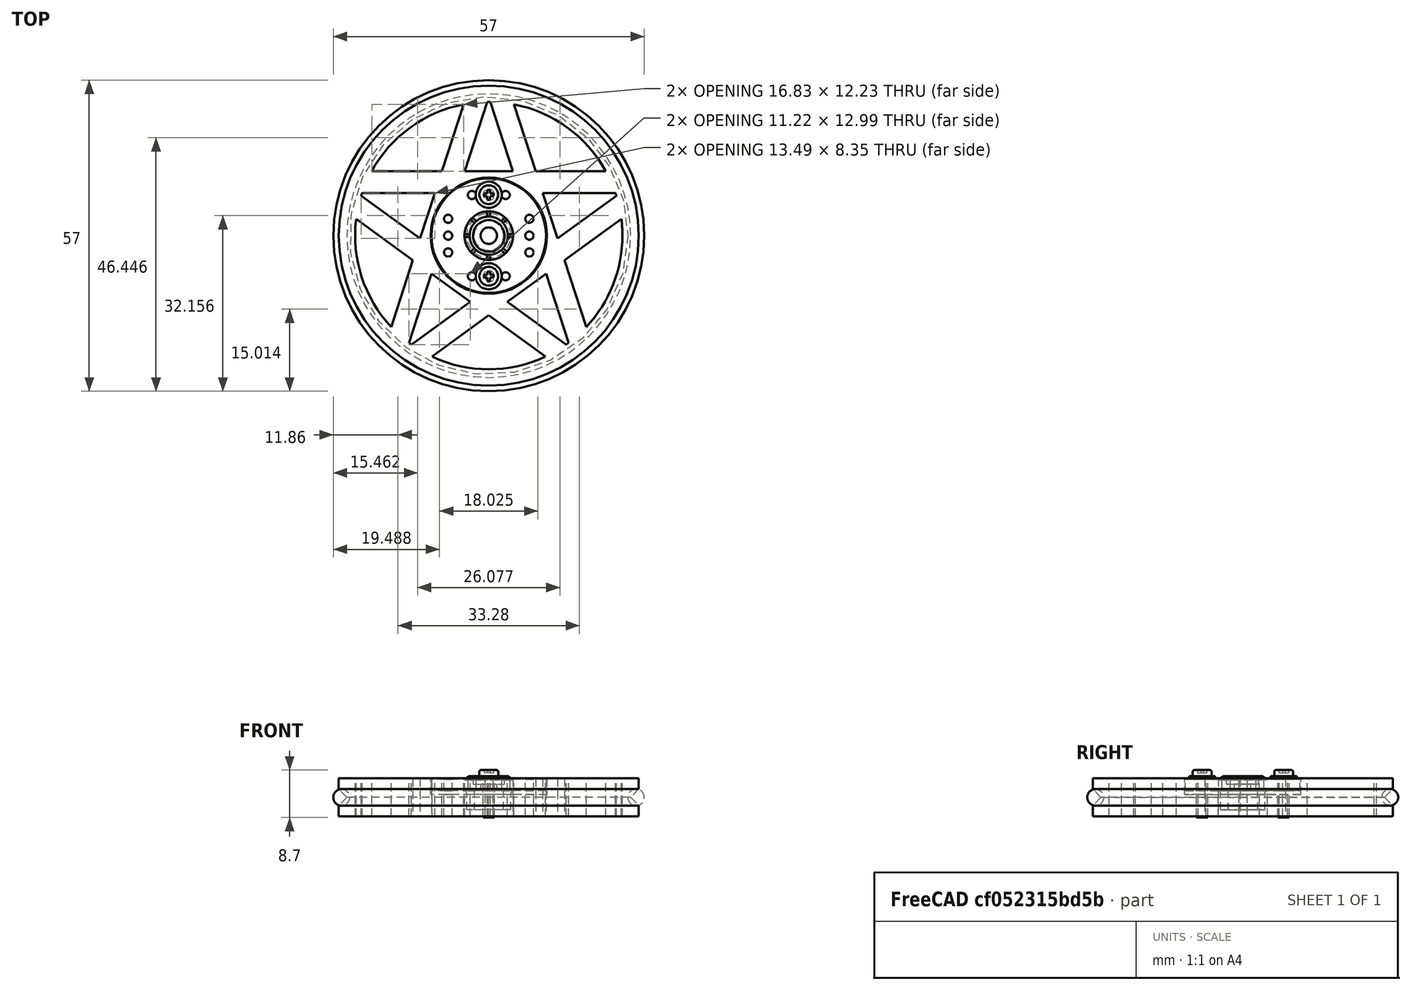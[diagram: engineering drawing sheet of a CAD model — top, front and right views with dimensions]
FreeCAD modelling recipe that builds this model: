
FCSTD DOCUMENT  (FreeCAD 0.14R3702 (Git))
Label: Miniskybot-wheel-pentacle-futaba3003-assembly
License: CC-BY 3.0
LicenseURL: http://creativecommons.org/licenses/by/3.0/
objects: Part::Feature×4, Part::Torus×1, Part::Compound×1
note: 6 computed .brp shape members not serialized (recipe doc carries the construction recipe); baked Part::Feature solids carry a one-line shape summary decoded from their .brp

FEATURE [Part::Feature] PolarPattern  label="Wheel-pentacle"
  shape: bbox 55 x 55 x 7 mm, 49 faces (baked)
FEATURE [Part::Torus] Torus  label="o-ring"
  Angle1 = -180
  Angle2 = 180
  Angle3 = 360
  Radius1 = 27
  Radius2 = 1.5
FEATURE [Part::Feature] Fillet  label="bolt-1"
  Placement = pos=(0,7.5,3.3) rot=(0,0,1;0rad)
  shape: bbox 4.8 x 4.8 x 8.7 mm, 21 faces (baked)
FEATURE [Part::Feature] Fillet001  label="servo-rounded-horn"
  Placement = pos=(0,0,-2.3) rot=(1,0,0;1.5708rad)
  shape: bbox 21 x 21 x 6.2 mm, 65 faces (baked)
FEATURE [Part::Feature] Fillet002  label="bolt-002"
  Placement = pos=(0,-7.45,3.3) rot=(0,0,1;0rad)
  shape: bbox 4.8 x 4.8 x 8.7 mm, 21 faces (baked)
FEATURE [Part::Compound] Compound  label="Miniskybot-wheel-pentacle-futaba3003-assembly-final"
  Links = -> [PolarPattern,Torus,Fillet001,Fillet,Fillet002]
